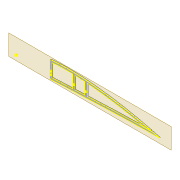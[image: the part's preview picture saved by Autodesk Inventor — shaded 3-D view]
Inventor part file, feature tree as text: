
AUTODESK INVENTOR PART (.ipt)
format: ipt  version: 2022 (Build 260153000, 153)  size: 343,040 bytes
history: native  units: mm
features: sketch x7, extrude x6, projected_geometry x5, shell x1, fillet x1, plane x1
ambient origin geometry x8: Origin, YZ Plane, XZ Plane, XY Plane, X Axis, Y Axis, Z Axis, Center Point
bodies: Solid1 (feature_tree)
feature tree (21):
  extrude  "Extrusion1"  Depth=4.0mm
  shell  "Shell1"  Thickness=5.0mm
  extrude  "Extrusion2"  Depth=2.0mm
  extrude  "Extrusion3"  Depth=5.9mm
  extrude  "Extrusion4"  Depth=10.0mm TaperAngle=0.0deg
  fillet  "Fillet1"  Radius=70.0mm
  plane  "Work Plane1"
  extrude  "Extrusion5"  Depth=2.0mm TaperAngle=0.0deg
  extrude  "Extrusion8"  Depth=5.0mm
  sketch  "Sketch17"  dims[d34=1.6mm d35=2.5mm d37=5.0mm d38=1.6mm d40=2.5mm d41=45.0mm d42=20.0mm d43=1.0mm d44=10.0mm d45=0.0mm d46=2.5mm d47=2.5mm]
  sketch  "Sketch3"  dims[d0=2.0mm d1=0.0mm d2=4.0mm d3=5.0mm]
  sketch  "Sketch7"  dims[d5=2.0mm d6=0.0mm d7=2.0mm]
  projected_geometry  "Projected Loop3"
  sketch  "Sketch8"  dims[d8=2.0mm d9=5.9mm]
  sketch  "Sketch9"  dims[d12=5.0mm d13=10.0mm d14=0.0mm d15=70.0mm]
  sketch  "Sketch10"  dims[d16=10.0mm d17=0.0mm d22=2.0mm d23=0.0mm]
  projected_geometry  "Projected Loop4"
  projected_geometry  "Projected Loop10"
  sketch  "Sketch16"  dims[d31=2.0mm d32=5.0mm]
  projected_geometry  "Projected Loop11"
  projected_geometry  "Project Cut Edges1"
